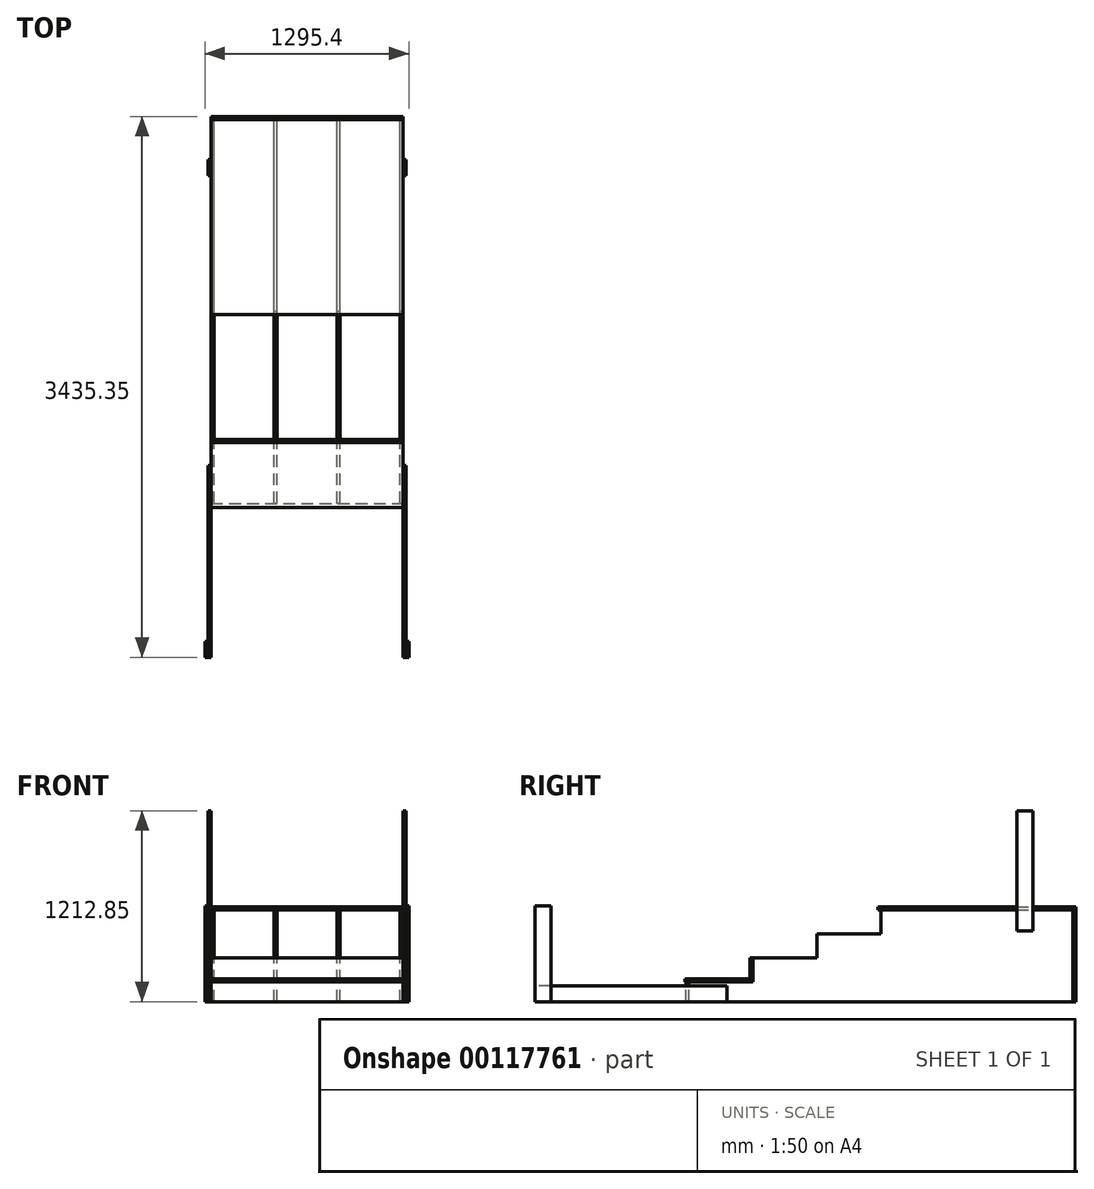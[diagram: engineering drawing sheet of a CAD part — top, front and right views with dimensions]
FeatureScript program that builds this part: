
annotation { "Feature Type Name" : "Feature", "Feature Type Description" : "" }
export const myFeature = defineFeature(function(context is Context, id is Id, definition is map)
    precondition{}
    {
        {
            var Q0;
            Q0=qCreatedBy(makeId("Right.planeOp"),FACE);
            var sketch = newSketch(context, id + "F0", { "sketchPlane" : qUnion([Q0])});
            skLineSegment(sketch, "E0", {"start": v(-787.4, 0) * mm, "end": v(1651, 0) * mm});
            skLineSegment(sketch, "E1", {"start": v(1651, 0) * mm, "end": v(1651, 584.2) * mm});
            skLineSegment(sketch, "E2.0", {"start": v(431.8, 584.2) * mm, "end": v(1651, 584.2) * mm});
            skLineSegment(sketch, "E2.1", {"start": v(431.8, 431.8) * mm, "end": v(431.8, 584.2) * mm});
            skLineSegment(sketch, "E2.2", {"start": v(25.4, 431.8) * mm, "end": v(431.8, 431.8) * mm});
            skLineSegment(sketch, "E2.3", {"start": v(25.4, 279.4) * mm, "end": v(25.4, 431.8) * mm});
            skLineSegment(sketch, "E2.4", {"start": v(-787.4, 0) * mm, "end": v(-787.4, 127) * mm});
            skLineSegment(sketch, "E2.5", {"start": v(-787.4, 127) * mm, "end": v(-381, 127) * mm});
            skLineSegment(sketch, "E2.6", {"start": v(-381, 127) * mm, "end": v(-381, 279.4) * mm});
            skLineSegment(sketch, "E2.7", {"start": v(-381, 279.4) * mm, "end": v(25.4, 279.4) * mm});
            skSolve(sketch);
        }
        {
            var Q0;
            Q0 = qSketchRegion(id + "F0", true);
            extrude(context, id + "F1", {"entities" : qUnion([Q0]), "depth" : 19.05 * mm});
        }
        {
            var Q0;
            Q0=makeQuery(id+"F1.opExtrude","SWEPT_BODY",BODY,{"disambiguationData":[OSD([sQuery(id+"F0.wireOp",EDGE,"E0"),sQuery(id+"F0.wireOp",EDGE,"E1"),sQuery(id+"F0.wireOp",EDGE,"E2.0"),sQuery(id+"F0.wireOp",EDGE,"E2.1"),sQuery(id+"F0.wireOp",EDGE,"E2.2"),sQuery(id+"F0.wireOp",EDGE,"E2.3"),sQuery(id+"F0.wireOp",EDGE,"E2.4"),sQuery(id+"F0.wireOp",EDGE,"E2.5"),sQuery(id+"F0.wireOp",EDGE,"E2.6"),sQuery(id+"F0.wireOp",EDGE,"E2.7")])]});
            transform(context, id + "F2", {"entities" : qUnion([Q0]), "transformType" : TransformType.TRANSLATION_3D, "dx" : 400.05 * mm, "dy" : 0 * mm, "dz" : 0 * mm, "makeCopy" : true});
        }
        {
            var Q0;
            Q0=makeQuery(id+"F1.opExtrude","SWEPT_BODY",BODY,{"disambiguationData":[OSD([sQuery(id+"F0.wireOp",EDGE,"E0"),sQuery(id+"F0.wireOp",EDGE,"E1"),sQuery(id+"F0.wireOp",EDGE,"E2.0"),sQuery(id+"F0.wireOp",EDGE,"E2.1"),sQuery(id+"F0.wireOp",EDGE,"E2.2"),sQuery(id+"F0.wireOp",EDGE,"E2.3"),sQuery(id+"F0.wireOp",EDGE,"E2.4"),sQuery(id+"F0.wireOp",EDGE,"E2.5"),sQuery(id+"F0.wireOp",EDGE,"E2.6"),sQuery(id+"F0.wireOp",EDGE,"E2.7")])]});
            transform(context, id + "F3", {"entities" : qUnion([Q0]), "transformType" : TransformType.TRANSLATION_3D, "dx" : -400.05 * mm, "dy" : 0 * mm, "dz" : 0 * mm, "makeCopy" : true});
        }
        {
            var Q0;
            Q0=makeQuery(id+"F3.opPattern","COPY",BODY,{"derivedFrom":makeQuery(id+"F1.opExtrude","SWEPT_BODY",BODY,{"disambiguationData":[OSD([sQuery(id+"F0.wireOp",EDGE,"E0"),sQuery(id+"F0.wireOp",EDGE,"E1"),sQuery(id+"F0.wireOp",EDGE,"E2.0"),sQuery(id+"F0.wireOp",EDGE,"E2.1"),sQuery(id+"F0.wireOp",EDGE,"E2.2"),sQuery(id+"F0.wireOp",EDGE,"E2.3"),sQuery(id+"F0.wireOp",EDGE,"E2.4"),sQuery(id+"F0.wireOp",EDGE,"E2.5"),sQuery(id+"F0.wireOp",EDGE,"E2.6"),sQuery(id+"F0.wireOp",EDGE,"E2.7")])]}),"instanceName":"1"});
            transform(context, id + "F4", {"entities" : qUnion([Q0]), "transformType" : TransformType.TRANSLATION_3D, "dx" : -400.05 * mm, "dy" : 0 * mm, "dz" : 0 * mm, "makeCopy" : true});
        }
        {
            var Q0;
            Q0=makeQuery(id+"F3.opPattern","COPY",FACE,{"derivedFrom":makeQuery(id+"F1.opExtrude","SWEPT_FACE",FACE,{"disambiguationData":[OSD([sQuery(id+"F0.wireOp",EDGE,"E2.5")])]}),"instanceName":"1"});
            var sketch = newSketch(context, id + "F5", { "sketchPlane" : qUnion([Q0])});
            skLineSegment(sketch, "E3.bottom", {"start": v(-800.1, -381) * mm, "end": v(419.1, -381) * mm});
            skLineSegment(sketch, "E3.top", {"start": v(-800.1, -812.8) * mm, "end": v(419.1, -812.8) * mm});
            skLineSegment(sketch, "E3.left", {"start": v(-800.1, -381) * mm, "end": v(-800.1, -812.8) * mm});
            skLineSegment(sketch, "E3.right", {"start": v(419.1, -381) * mm, "end": v(419.1, -812.8) * mm});
            skSolve(sketch);
        }
        {
            var Q0;
            Q0 = qSketchRegion(id + "F5", true);
            extrude(context, id + "F6", {"entities" : qUnion([Q0]), "depth" : 19.05 * mm});
        }
        {
            var Q0;
            Q0=makeQuery(id+"F3.opPattern","COPY",FACE,{"derivedFrom":makeQuery(id+"F1.opExtrude","SWEPT_FACE",FACE,{"disambiguationData":[OSD([sQuery(id+"F0.wireOp",EDGE,"E2.4")])]}),"instanceName":"1"});
            var sketch = newSketch(context, id + "F7", { "sketchPlane" : qUnion([Q0])});
            skLineSegment(sketch, "E4.bottom", {"start": v(-800.1, 0) * mm, "end": v(419.1, 0) * mm});
            skLineSegment(sketch, "E4.top", {"start": v(-800.1, 127) * mm, "end": v(419.1, 127) * mm});
            skLineSegment(sketch, "E4.left", {"start": v(-800.1, 0) * mm, "end": v(-800.1, 127) * mm});
            skLineSegment(sketch, "E4.right", {"start": v(419.1, 0) * mm, "end": v(419.1, 127) * mm});
            skSolve(sketch);
        }
        {
            var Q0;
            Q0 = qSketchRegion(id + "F7", true);
            extrude(context, id + "F8", {"entities" : qUnion([Q0]), "depth" : 19.05 * mm});
        }
        {
            var Q0;
            Q0=makeQuery(id+"F3.opPattern","COPY",FACE,{"derivedFrom":makeQuery(id+"F1.opExtrude","SWEPT_FACE",FACE,{"disambiguationData":[OSD([sQuery(id+"F0.wireOp",EDGE,"E2.0")])]}),"instanceName":"1"});
            var sketch = newSketch(context, id + "F9", { "sketchPlane" : qUnion([Q0])});
            skLineSegment(sketch, "E5.bottom", {"start": v(-800.1, 412.75) * mm, "end": v(419.1, 412.75) * mm});
            skLineSegment(sketch, "E5.top", {"start": v(-800.1, 1651) * mm, "end": v(419.1, 1651) * mm});
            skLineSegment(sketch, "E5.left", {"start": v(-800.1, 412.75) * mm, "end": v(-800.1, 1651) * mm});
            skLineSegment(sketch, "E5.right", {"start": v(419.1, 412.75) * mm, "end": v(419.1, 1651) * mm});
            skSolve(sketch);
        }
        {
            var Q0;
            Q0 = qSketchRegion(id + "F9", true);
            extrude(context, id + "F10", {"entities" : qUnion([Q0]), "depth" : 19.05 * mm});
        }
        {
            var Q0;
            Q0=makeQuery(id+"F2.opPattern","COPY",FACE,{"derivedFrom":makeQuery(id+"F1.opExtrude","SWEPT_FACE",FACE,{"disambiguationData":[OSD([sQuery(id+"F0.wireOp",EDGE,"E1")])]}),"instanceName":"1"});
            var sketch = newSketch(context, id + "F11", { "sketchPlane" : qUnion([Q0])});
            skLineSegment(sketch, "E6.bottom", {"start": v(-419.1, 603.25) * mm, "end": v(800.1, 603.25) * mm});
            skLineSegment(sketch, "E6.top", {"start": v(-419.1, 0) * mm, "end": v(800.1, 0) * mm});
            skLineSegment(sketch, "E6.left", {"start": v(-419.1, 603.25) * mm, "end": v(-419.1, 0) * mm});
            skLineSegment(sketch, "E6.right", {"start": v(800.1, 603.25) * mm, "end": v(800.1, 0) * mm});
            skSolve(sketch);
        }
        {
            var Q0;
            Q0 = qSketchRegion(id + "F11", true);
            extrude(context, id + "F12", {"entities" : qUnion([Q0]), "depth" : 19.05 * mm});
        }
        {
            var Q0;
            Q0=makeQuery(id+"F2.opPattern","COPY",FACE,{"derivedFrom":makeQuery(id+"F1.opExtrude","CAP_FACE",FACE,{"disambiguationData":[OSD([sQuery(id+"F0.wireOp",EDGE,"E0"),sQuery(id+"F0.wireOp",EDGE,"E1"),sQuery(id+"F0.wireOp",EDGE,"E2.0"),sQuery(id+"F0.wireOp",EDGE,"E2.1"),sQuery(id+"F0.wireOp",EDGE,"E2.2"),sQuery(id+"F0.wireOp",EDGE,"E2.3"),sQuery(id+"F0.wireOp",EDGE,"E2.4"),sQuery(id+"F0.wireOp",EDGE,"E2.5"),sQuery(id+"F0.wireOp",EDGE,"E2.6"),sQuery(id+"F0.wireOp",EDGE,"E2.7")])],"isStart":false}),"instanceName":"1"});
            var sketch = newSketch(context, id + "F13", { "sketchPlane" : qUnion([Q0])});
            skLineSegment(sketch, "E7.bottom", {"start": v(1295.4, 450.85) * mm, "end": v(1397, 450.85) * mm});
            skLineSegment(sketch, "E7.top", {"start": v(1295.4, 1212.85) * mm, "end": v(1397, 1212.85) * mm});
            skLineSegment(sketch, "E7.left", {"start": v(1295.4, 450.85) * mm, "end": v(1295.4, 1212.85) * mm});
            skLineSegment(sketch, "E7.right", {"start": v(1397, 450.85) * mm, "end": v(1397, 1212.85) * mm});
            skPoint(sketch, "E8", {"position": v(1346.2, 1212.85) * mm});
            skSolve(sketch);
        }
        {
            var Q0;
            Q0 = qSketchRegion(id + "F13", true);
            extrude(context, id + "F14", {"entities" : qUnion([Q0]), "depth" : 19.05 * mm});
        }
        {
            var Q0;
            Q0=makeQuery(id+"F2.opPattern","COPY",FACE,{"derivedFrom":makeQuery(id+"F1.opExtrude","CAP_FACE",FACE,{"disambiguationData":[OSD([sQuery(id+"F0.wireOp",EDGE,"E0"),sQuery(id+"F0.wireOp",EDGE,"E1"),sQuery(id+"F0.wireOp",EDGE,"E2.0"),sQuery(id+"F0.wireOp",EDGE,"E2.1"),sQuery(id+"F0.wireOp",EDGE,"E2.2"),sQuery(id+"F0.wireOp",EDGE,"E2.3"),sQuery(id+"F0.wireOp",EDGE,"E2.4"),sQuery(id+"F0.wireOp",EDGE,"E2.5"),sQuery(id+"F0.wireOp",EDGE,"E2.6"),sQuery(id+"F0.wireOp",EDGE,"E2.7")])],"isStart":false}),"instanceName":"1"});
            var Q1;
            Q1=makeQuery(id+"F4.opPattern","COPY",FACE,{"derivedFrom":makeQuery(id+"F3.opPattern","COPY",FACE,{"derivedFrom":makeQuery(id+"F1.opExtrude","CAP_FACE",FACE,{"disambiguationData":[OSD([sQuery(id+"F0.wireOp",EDGE,"E0"),sQuery(id+"F0.wireOp",EDGE,"E1"),sQuery(id+"F0.wireOp",EDGE,"E2.0"),sQuery(id+"F0.wireOp",EDGE,"E2.1"),sQuery(id+"F0.wireOp",EDGE,"E2.2"),sQuery(id+"F0.wireOp",EDGE,"E2.3"),sQuery(id+"F0.wireOp",EDGE,"E2.4"),sQuery(id+"F0.wireOp",EDGE,"E2.5"),sQuery(id+"F0.wireOp",EDGE,"E2.6"),sQuery(id+"F0.wireOp",EDGE,"E2.7")])],"isStart":true}),"instanceName":"1"}),"instanceName":"1"});
            cPlane(context, id + "F15", {"entities" : qUnion([Q0, Q1]), "cplaneType" : CPlaneType.MID_PLANE, "offset" : 25.4 * mm, "width" : 152.4 * mm, "height" : 152.4 * mm});
        }
        {
            var Q0;
            Q0=makeQuery(id+"F14.opExtrude","SWEPT_BODY",BODY,{"disambiguationData":[OSD([sQuery(id+"F13.wireOp",EDGE,"E7.bottom"),sQuery(id+"F13.wireOp",EDGE,"E7.top"),sQuery(id+"F13.wireOp",EDGE,"E7.left"),sQuery(id+"F13.wireOp",EDGE,"E7.right")])]});
            var Q1;
            Q1=qCreatedBy(id+"F15.planeOp",FACE);
            mirror(context, id + "F16", {"entities" : qUnion([Q0]), "mirrorPlane" : qUnion([Q1])});
        }
        {
            var Q0;
            Q0=makeQuery(id+"F2.opPattern","COPY",FACE,{"derivedFrom":makeQuery(id+"F1.opExtrude","CAP_FACE",FACE,{"disambiguationData":[OSD([sQuery(id+"F0.wireOp",EDGE,"E0"),sQuery(id+"F0.wireOp",EDGE,"E1"),sQuery(id+"F0.wireOp",EDGE,"E2.0"),sQuery(id+"F0.wireOp",EDGE,"E2.1"),sQuery(id+"F0.wireOp",EDGE,"E2.2"),sQuery(id+"F0.wireOp",EDGE,"E2.3"),sQuery(id+"F0.wireOp",EDGE,"E2.4"),sQuery(id+"F0.wireOp",EDGE,"E2.5"),sQuery(id+"F0.wireOp",EDGE,"E2.6"),sQuery(id+"F0.wireOp",EDGE,"E2.7")])],"isStart":false}),"instanceName":"1"});
            var sketch = newSketch(context, id + "F17", { "sketchPlane" : qUnion([Q0])});
            skLineSegment(sketch, "E9.bottom", {"start": v(-546.1, 0) * mm, "end": v(-1765.3, 0) * mm});
            skLineSegment(sketch, "E9.top", {"start": v(-546.1, 101.6) * mm, "end": v(-1765.3, 101.6) * mm});
            skLineSegment(sketch, "E9.left", {"start": v(-546.1, 0) * mm, "end": v(-546.1, 101.6) * mm});
            skLineSegment(sketch, "E9.right", {"start": v(-1765.3, 0) * mm, "end": v(-1765.3, 101.6) * mm});
            skSolve(sketch);
        }
        {
            var Q0;
            Q0 = qSketchRegion(id + "F17", true);
            extrude(context, id + "F18", {"entities" : qUnion([Q0]), "depth" : 19.05 * mm});
        }
        {
            var Q0;
            Q0=makeQuery(id+"F18.opExtrude","CAP_FACE",FACE,{"disambiguationData":[OSD([sQuery(id+"F17.wireOp",EDGE,"E9.bottom"),sQuery(id+"F17.wireOp",EDGE,"E9.top"),sQuery(id+"F17.wireOp",EDGE,"E9.left"),sQuery(id+"F17.wireOp",EDGE,"E9.right")])],"isStart":false});
            var sketch = newSketch(context, id + "F19", { "sketchPlane" : qUnion([Q0])});
            skLineSegment(sketch, "E10.bottom", {"start": v(-1765.3, 0) * mm, "end": v(-1663.7, 0) * mm});
            skLineSegment(sketch, "E10.top", {"start": v(-1765.3, 609.6) * mm, "end": v(-1663.7, 609.6) * mm});
            skLineSegment(sketch, "E10.left", {"start": v(-1765.3, 0) * mm, "end": v(-1765.3, 609.6) * mm});
            skLineSegment(sketch, "E10.right", {"start": v(-1663.7, 0) * mm, "end": v(-1663.7, 609.6) * mm});
            skSolve(sketch);
        }
        {
            var Q0;
            Q0 = qSketchRegion(id + "F19", true);
            extrude(context, id + "F20", {"entities" : qUnion([Q0]), "depth" : 19.05 * mm});
        }
        {
            var Q0;
            Q0=makeQuery(id+"F18.opExtrude","SWEPT_BODY",BODY,{"disambiguationData":[OSD([sQuery(id+"F17.wireOp",EDGE,"E9.bottom"),sQuery(id+"F17.wireOp",EDGE,"E9.top"),sQuery(id+"F17.wireOp",EDGE,"E9.left"),sQuery(id+"F17.wireOp",EDGE,"oQbL1Plm-WJ51-H7HF-y3XE-xLJnq5cljBjm.bottom"),sQuery(id+"F17.wireOp",EDGE,"oQbL1Plm-WJ51-H7HF-y3XE-xLJnq5cljBjm.top"),sQuery(id+"F17.wireOp",EDGE,"oQbL1Plm-WJ51-H7HF-y3XE-xLJnq5cljBjm.left"),sQuery(id+"F17.wireOp",EDGE,"oQbL1Plm-WJ51-H7HF-y3XE-xLJnq5cljBjm.right")])]});
            var Q1;
            Q1=makeQuery(id+"F20.opExtrude","SWEPT_BODY",BODY,{"disambiguationData":[OSD([sQuery(id+"F19.wireOp",EDGE,"E10.bottom"),sQuery(id+"F19.wireOp",EDGE,"E10.top"),sQuery(id+"F19.wireOp",EDGE,"E10.left"),sQuery(id+"F19.wireOp",EDGE,"E10.right")])]});
            var Q2;
            Q2=qCreatedBy(id+"F15.planeOp",FACE);
            mirror(context, id + "F21", {"entities" : qUnion([Q0, Q1]), "mirrorPlane" : qUnion([Q2])});
        }
        {
            var Q0;
            Q0=makeQuery(id+"F3.opPattern","COPY",FACE,{"derivedFrom":makeQuery(id+"F1.opExtrude","SWEPT_FACE",FACE,{"disambiguationData":[OSD([sQuery(id+"F0.wireOp",EDGE,"E2.6")])]}),"instanceName":"1"});
            var sketch = newSketch(context, id + "F22", { "sketchPlane" : qUnion([Q0])});
            skLineSegment(sketch, "E11.bottom", {"start": v(-800.1, 279.4) * mm, "end": v(419.1, 279.4) * mm});
            skLineSegment(sketch, "E11.top", {"start": v(-800.1, 146.05) * mm, "end": v(419.1, 146.05) * mm});
            skLineSegment(sketch, "E11.left", {"start": v(-800.1, 279.4) * mm, "end": v(-800.1, 146.05) * mm});
            skLineSegment(sketch, "E11.right", {"start": v(419.1, 279.4) * mm, "end": v(419.1, 146.05) * mm});
            skSolve(sketch);
        }
        {
            var Q0;
            Q0 = qSketchRegion(id + "F22", true);
            extrude(context, id + "F23", {"entities" : qUnion([Q0]), "depth" : 19.05 * mm});
        }
    });
